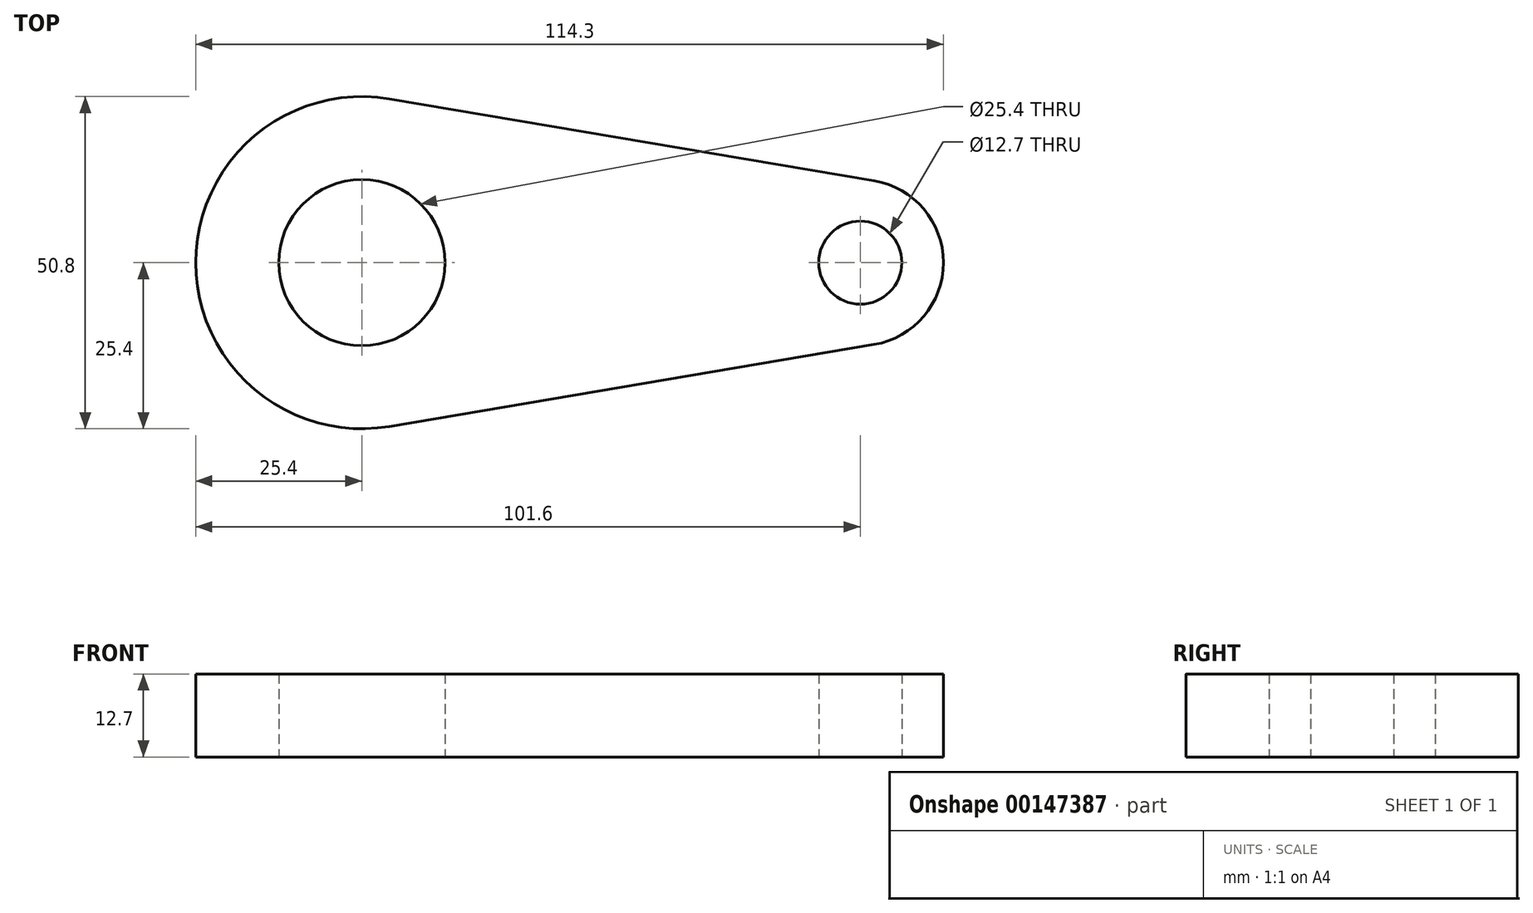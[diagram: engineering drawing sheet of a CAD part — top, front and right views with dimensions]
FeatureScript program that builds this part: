
annotation { "Feature Type Name" : "Feature", "Feature Type Description" : "" }
export const myFeature = defineFeature(function(context is Context, id is Id, definition is map)
    precondition{}
    {
        {
            var Q0;
            Q0=qCreatedBy(makeId("Top.planeOp"),FACE);
            var sketch = newSketch(context, id + "F0", { "sketchPlane" : qUnion([Q0])});
            skArc(sketch, "E0", {"start": v(4.23, 25.04) * mm, "mid": v(-25.4, 0) * mm, "end": v(4.23, -25.04) * mm});
            skArc(sketch, "E1", {"start": v(78.32, -12.52) * mm, "mid": v(88.9, 0) * mm, "end": v(78.32, 12.52) * mm});
            skLineSegment(sketch, "E2", {"start": v(4.23, 25.04) * mm, "end": v(78.32, 12.52) * mm});
            skLineSegment(sketch, "E3", {"start": v(4.23, -25.04) * mm, "end": v(78.32, -12.52) * mm});
            skCircle(sketch, "E4", {"center": v(0, 0) * mm, "radius": 12.7 * mm});
            skCircle(sketch, "E5", {"center": v(76.2, 0) * mm, "radius": 6.35 * mm});
            skSolve(sketch);
        }
        {
            var Q0;
            Q0 = qSketchRegion(id + "F0", true);
            extrude(context, id + "F1", {"entities" : qUnion([Q0]), "depth" : 12.7 * mm});
        }
    });
